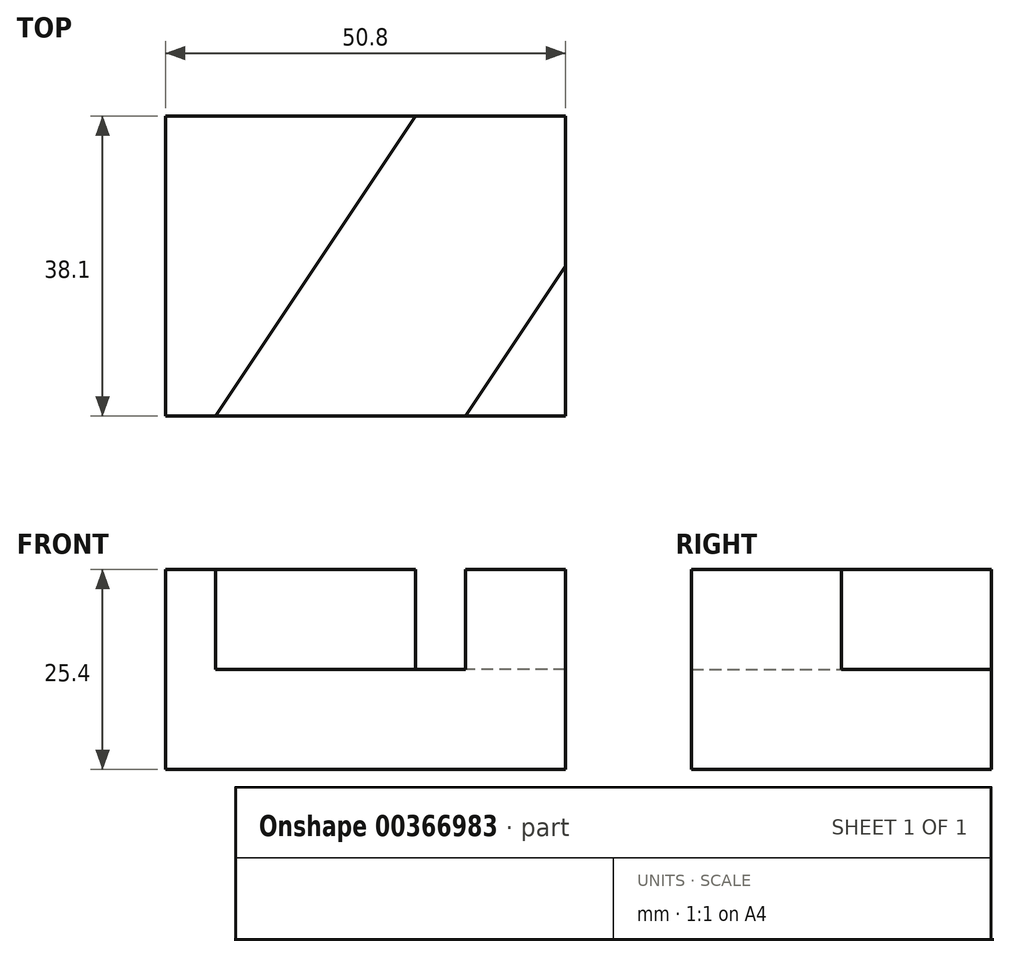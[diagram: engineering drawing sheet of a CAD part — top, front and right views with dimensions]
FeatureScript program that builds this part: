
annotation { "Feature Type Name" : "Feature", "Feature Type Description" : "" }
export const myFeature = defineFeature(function(context is Context, id is Id, definition is map)
    precondition{}
    {
        {
            var Q0;
            Q0=qCreatedBy(makeId("Front.planeOp"),FACE);
            var sketch = newSketch(context, id + "F0", { "sketchPlane" : qUnion([Q0])});
            skLineSegment(sketch, "E0", {"start": v(0, 0) * mm, "end": v(50.8, 0) * mm});
            skLineSegment(sketch, "E1", {"start": v(50.8, 0) * mm, "end": v(50.8, 12.7) * mm});
            skLineSegment(sketch, "E2", {"start": v(50.8, 12.7) * mm, "end": v(0, 12.7) * mm});
            skLineSegment(sketch, "E3", {"start": v(0, 12.7) * mm, "end": v(0, 0) * mm});
            skSolve(sketch);
        }
        {
            var Q0;
            Q0=makeQuery(id+"F0.imprint","IMPRINT",FACE,{"disambiguationData":[TD([[makeQuery(id+"F0.imprint","IMPRINT",EDGE,{"derivedFrom":sQuery(id+"F0.wireOp",EDGE,"E0")}),1.0]])]});
            extrude(context, id + "F1", {"entities" : qUnion([Q0]), "depth" : 38.1 * mm});
        }
        {
            var Q0;
            Q0=makeQuery(id+"F1.opExtrude","SWEPT_FACE",FACE,{"disambiguationData":[OSD([sQuery(id+"F0.wireOp",EDGE,"E2")])]});
            var sketch = newSketch(context, id + "F2", { "sketchPlane" : qUnion([Q0])});
            skLineSegment(sketch, "E4", {"start": v(50.8, -19.05) * mm, "end": v(38.1, -38.1) * mm});
            skSolve(sketch);
        }
        {
            var Q0;
            {var subQ0=sQuery(id+"F2.wireOp",EDGE,"E4");Q0=makeQuery(id+"F2.imprint","IMPRINT",FACE,{"disambiguationData":[TD([[makeQuery(id+"F2.imprint","IMPRINT",EDGE,{"derivedFrom":subQ0}),1.0]])]});}
            extrude(context, id + "F3", {"entities" : qUnion([Q0]), "operationType" : NewBodyOperationType.ADD, "depth" : 12.7 * mm});
        }
        {
            var Q0;
            Q0=makeQuery(id+"F1.opExtrude","SWEPT_FACE",FACE,{"disambiguationData":[OSD([sQuery(id+"F0.wireOp",EDGE,"E2")])]});
            var sketch = newSketch(context, id + "F4", { "sketchPlane" : qUnion([Q0])});
            skLineSegment(sketch, "E5", {"start": v(6.35, 0) * mm, "end": v(6.35, -38.1) * mm});
            skSolve(sketch);
        }
        {
            var Q0;
            {var subQ0=sQuery(id+"F4.wireOp",EDGE,"E5");Q0=makeQuery(id+"F4.imprint","IMPRINT",FACE,{"disambiguationData":[TD([[makeQuery(id+"F4.imprint","IMPRINT",EDGE,{"derivedFrom":subQ0}),-1.0]])]});}
            extrude(context, id + "F5", {"entities" : qUnion([Q0]), "operationType" : NewBodyOperationType.ADD, "depth" : 12.7 * mm});
        }
        {
            var Q0;
            Q0=makeQuery(id+"F1.opExtrude","SWEPT_FACE",FACE,{"disambiguationData":[OSD([sQuery(id+"F0.wireOp",EDGE,"E2")])]});
            var sketch = newSketch(context, id + "F6", { "sketchPlane" : qUnion([Q0])});
            skLineSegment(sketch, "E6", {"start": v(6.35, -38.1) * mm, "end": v(31.75, 0) * mm});
            skSolve(sketch);
        }
        {
            var Q0;
            {var subQ0=sQuery(id+"F6.wireOp",EDGE,"E6");Q0=makeQuery(id+"F6.imprint","IMPRINT",FACE,{"disambiguationData":[TD([[makeQuery(id+"F6.imprint","IMPRINT",EDGE,{"derivedFrom":subQ0}),1.0]])]});}
            extrude(context, id + "F7", {"entities" : qUnion([Q0]), "operationType" : NewBodyOperationType.ADD, "depth" : 12.7 * mm});
        }
    });
